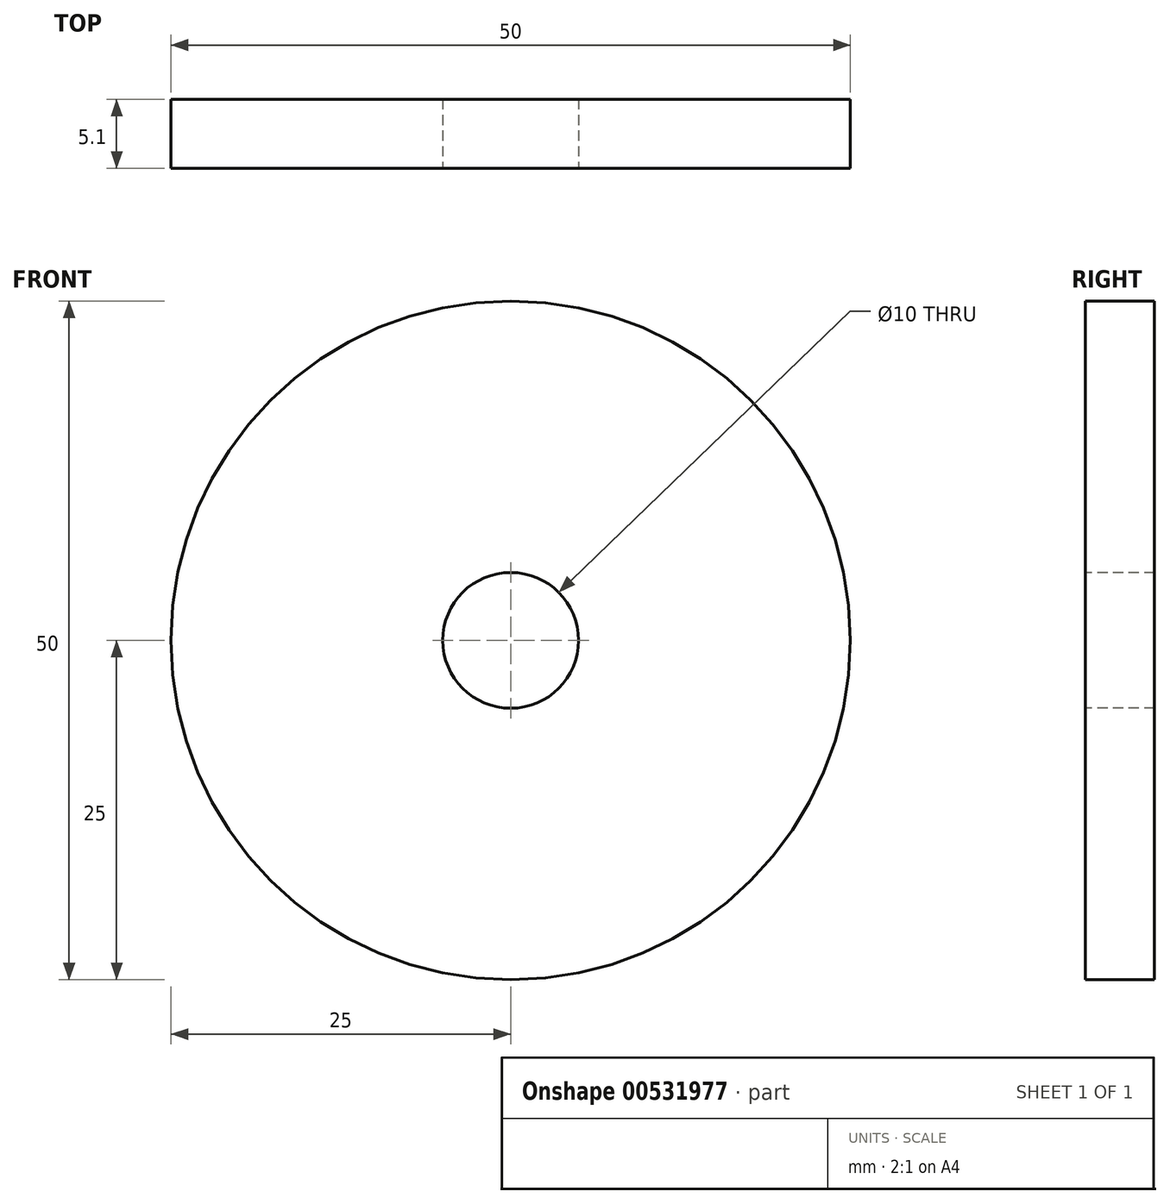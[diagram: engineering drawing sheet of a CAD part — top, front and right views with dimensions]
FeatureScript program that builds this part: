
annotation { "Feature Type Name" : "Feature", "Feature Type Description" : "" }
export const myFeature = defineFeature(function(context is Context, id is Id, definition is map)
    precondition{}
    {
        {
            var Q0;
            Q0=qCreatedBy(makeId("Front.planeOp"),FACE);
            var sketch = newSketch(context, id + "F0", { "sketchPlane" : qUnion([Q0])});
            skCircle(sketch, "E0", {"center": v(0, 0) * mm, "radius": 25 * mm});
            skSolve(sketch);
        }
        {
            var Q0;
            Q0=makeQuery(id+"F0.imprint","IMPRINT",FACE,{"disambiguationData":[TD([[makeQuery(id+"F0.imprint","IMPRINT",EDGE,{"derivedFrom":sQuery(id+"F0.wireOp",EDGE,"E0")}),1.0]])]});
            extrude(context, id + "F1", {"entities" : qUnion([Q0]), "depth" : 5.1 * mm, "offsetDistance" : 25 * mm});
        }
        {
            var Q0;
            Q0=makeQuery(id+"F1.opExtrude","CAP_FACE",FACE,{"disambiguationData":[OSD([sQuery(id+"F0.wireOp",EDGE,"E0")])],"isStart":false});
            var sketch = newSketch(context, id + "F2", { "sketchPlane" : qUnion([Q0])});
            skCircle(sketch, "E1", {"center": v(0, 0) * mm, "radius": 5 * mm});
            skSolve(sketch);
        }
        {
            var Q0;
            Q0=makeQuery(id+"F2.imprint","IMPRINT",FACE,{"disambiguationData":[TD([[makeQuery(id+"F2.imprint","IMPRINT",EDGE,{"derivedFrom":sQuery(id+"F2.wireOp",EDGE,"E1")}),1.0]])]});
            extrude(context, id + "F3", {"entities" : qUnion([Q0]), "operationType" : NewBodyOperationType.REMOVE, "endBound" : BoundingType.THROUGH_ALL, "oppositeDirection" : true, "depth" : 25 * mm, "offsetDistance" : 25 * mm});
        }
    });
